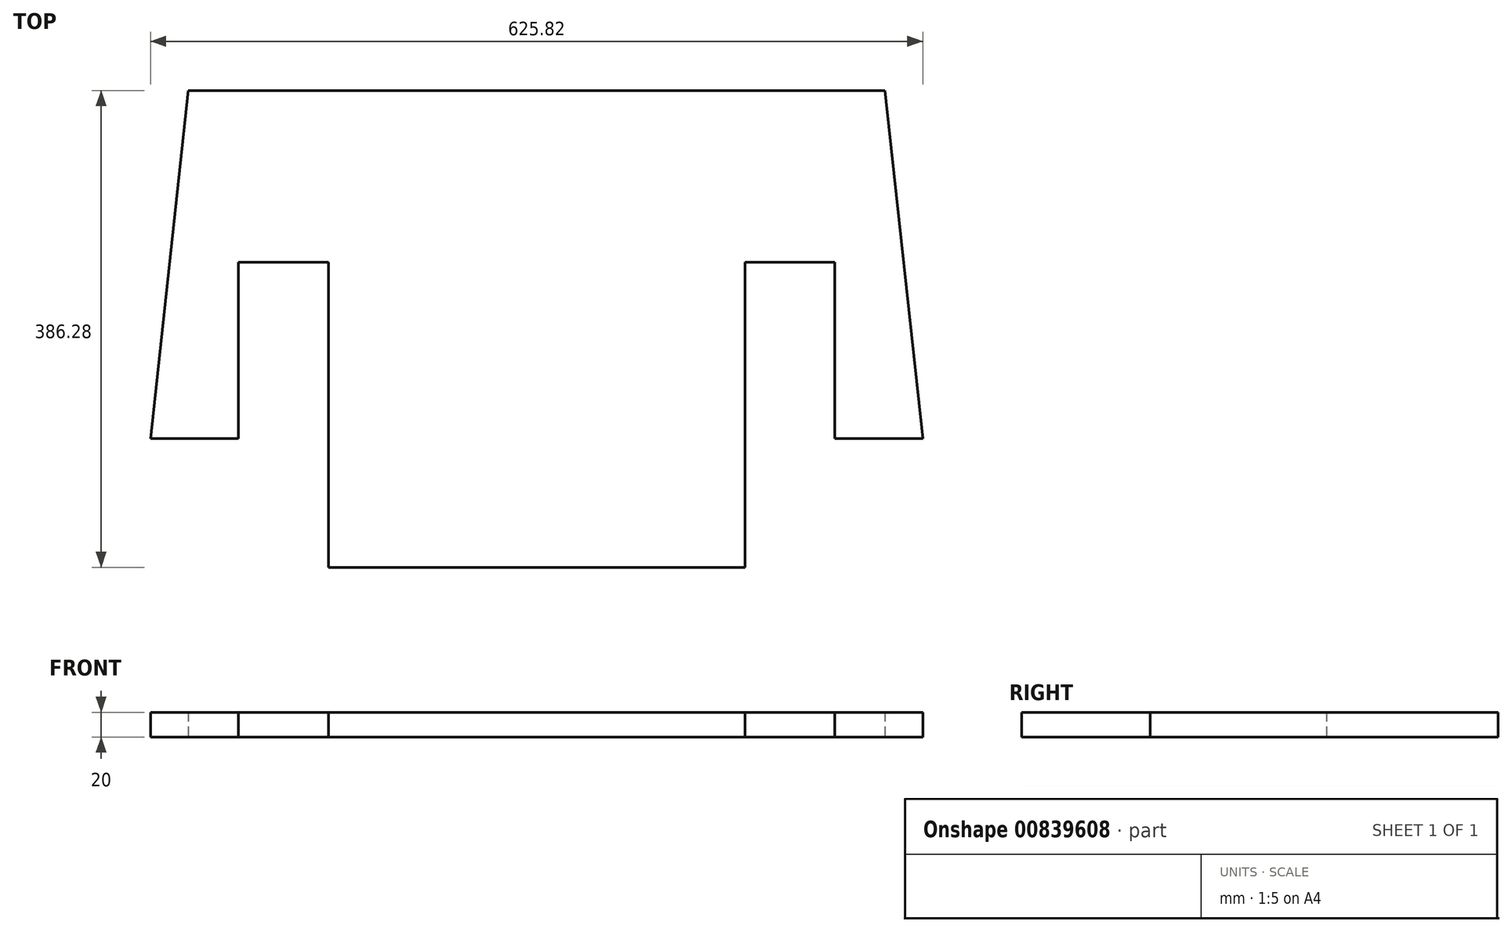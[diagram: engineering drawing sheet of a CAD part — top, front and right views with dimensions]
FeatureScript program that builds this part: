
annotation { "Feature Type Name" : "Feature", "Feature Type Description" : "" }
export const myFeature = defineFeature(function(context is Context, id is Id, definition is map)
    precondition{}
    {
        {
            var Q0;
            Q0=qCreatedBy(makeId("Top.planeOp"),FACE);
            var sketch = newSketch(context, id + "F0", { "sketchPlane" : qUnion([Q0])});
            skLineSegment(sketch, "E0", {"start": v(0, 0) * mm, "end": v(0, 386.28) * mm});
            skLineSegment(sketch, "E1", {"start": v(0, 386.28) * mm, "end": v(-282.29, 386.28) * mm});
            skLineSegment(sketch, "E2", {"start": v(-282.29, 386.28) * mm, "end": v(-312.91, 104.29) * mm});
            skLineSegment(sketch, "E3", {"start": v(-312.91, 104.29) * mm, "end": v(-241.6, 104.29) * mm});
            skLineSegment(sketch, "E4", {"start": v(-241.6, 104.29) * mm, "end": v(-241.6, 247.18) * mm});
            skLineSegment(sketch, "E5", {"start": v(-241.6, 247.18) * mm, "end": v(-168.72, 247.18) * mm});
            skLineSegment(sketch, "E6", {"start": v(-168.72, 247.18) * mm, "end": v(-168.72, 0) * mm});
            skLineSegment(sketch, "E7", {"start": v(-168.72, 0) * mm, "end": v(0, 0) * mm});
            skSolve(sketch);
        }
        {
            var Q0;
            Q0=makeQuery(id+"F0.imprint","IMPRINT",FACE,{"disambiguationData":[TD([[makeQuery(id+"F0.imprint","IMPRINT",EDGE,{"derivedFrom":sQuery(id+"F0.wireOp",EDGE,"E0")}),1.0]])]});
            extrude(context, id + "F1", {"entities" : qUnion([Q0]), "depth" : 20 * mm, "offsetDistance" : 25 * mm});
        }
        {
            var Q0;
            Q0=makeQuery(id+"F1.opExtrude","SWEPT_BODY",BODY,{"disambiguationData":[OSD([sQuery(id+"F0.wireOp",EDGE,"E0"),sQuery(id+"F0.wireOp",EDGE,"E1"),sQuery(id+"F0.wireOp",EDGE,"E2"),sQuery(id+"F0.wireOp",EDGE,"E3"),sQuery(id+"F0.wireOp",EDGE,"E4"),sQuery(id+"F0.wireOp",EDGE,"E5"),sQuery(id+"F0.wireOp",EDGE,"E6"),sQuery(id+"F0.wireOp",EDGE,"E7")])]});
            var Q1;
            Q1=qCreatedBy(makeId("Right.planeOp"),FACE);
            mirror(context, id + "F2", {"operationType" : NewBodyOperationType.ADD, "entities" : qUnion([Q0]), "mirrorPlane" : qUnion([Q1])});
        }
    });
